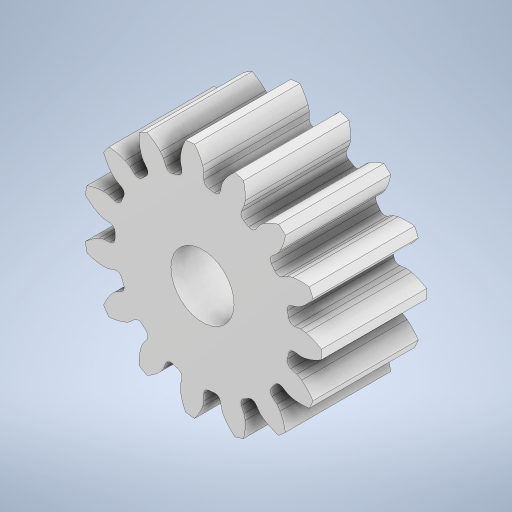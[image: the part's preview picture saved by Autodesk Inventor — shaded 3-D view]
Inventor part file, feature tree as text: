
AUTODESK INVENTOR PART (.ipt)
format: ipt  version: 2023 (Build 270158000, 158)  size: 455,680 bytes
history: native  units: in
note: dims shown in document units (in); Inventor stores cm internally (conversion verified against a paired STEP export)
features: extrude x1, sketch x1, imported_body x1
ambient origin geometry x8: Origin, YZ Plane, XZ Plane, XY Plane, X Axis, Y Axis, Z Axis, Center Point
bodies: Solid1 (feature_tree)
feature tree (3):
  extrude  "Extrusion1"  Depth=0.3937in TaperAngle=0.0deg
  sketch  "Sketch1"  dims[d0=0.2362in d1=0.3937in d2=0.0in]
  imported_body  "Base1"
